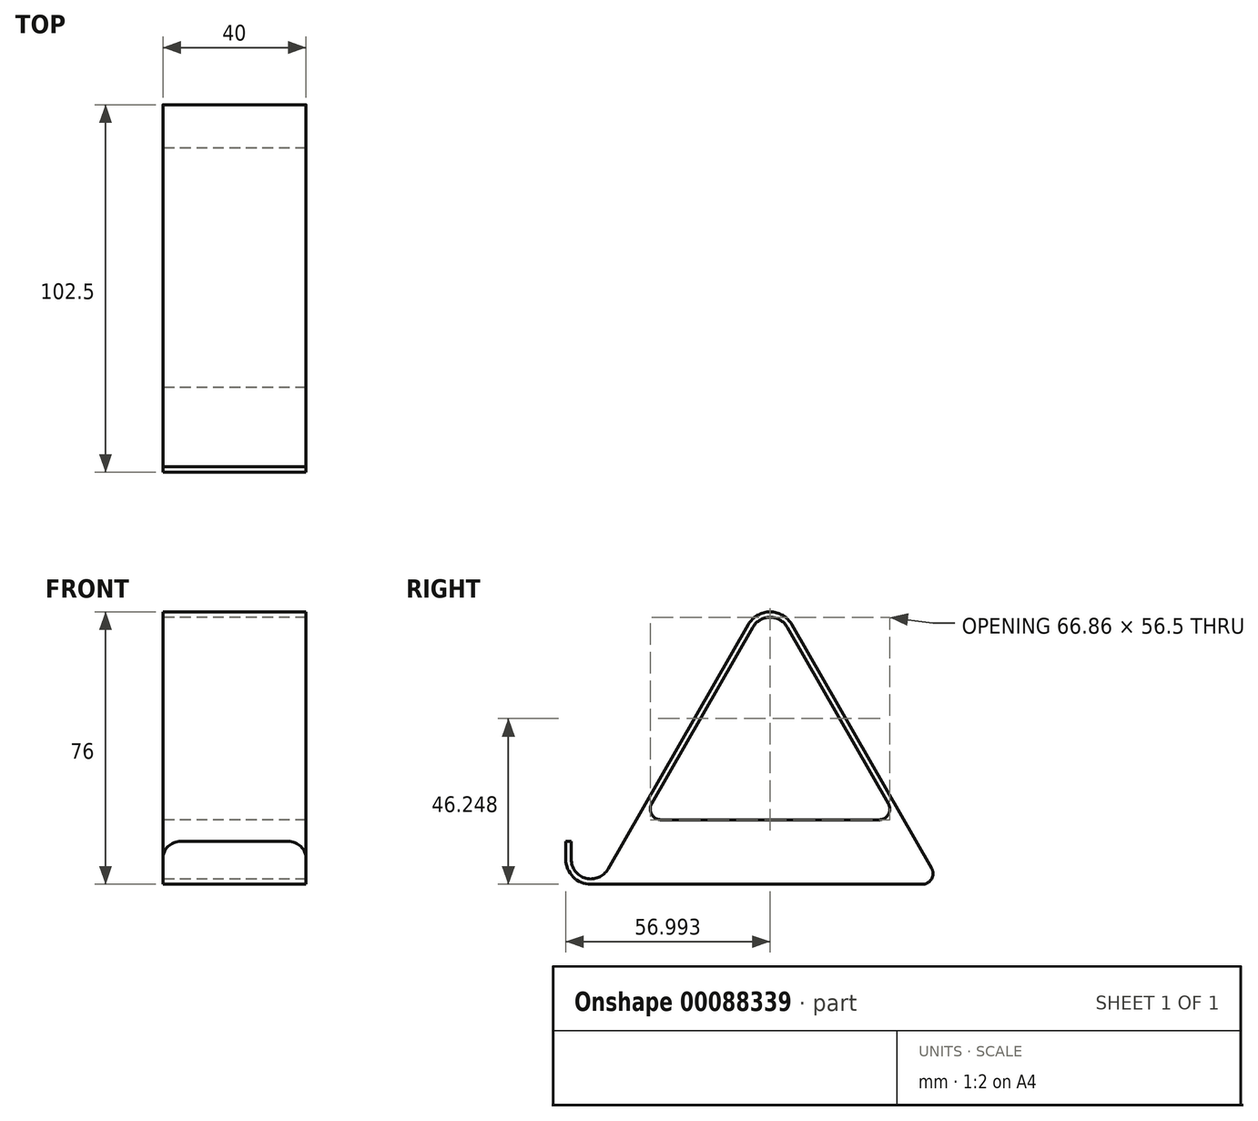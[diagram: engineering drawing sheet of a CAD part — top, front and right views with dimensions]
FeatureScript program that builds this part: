
annotation { "Feature Type Name" : "Feature", "Feature Type Description" : "" }
export const myFeature = defineFeature(function(context is Context, id is Id, definition is map)
    precondition{}
    {
        {
            var Q0;
            Q0=qCreatedBy(makeId("Right.planeOp"),FACE);
            var sketch = newSketch(context, id + "F0", { "sketchPlane" : qUnion([Q0])});
            skArc(sketch, "E0", {"start": v(54.77, 64.74) * mm, "mid": v(50, 67.5) * mm, "end": v(45.23, 64.74) * mm});
            skArc(sketch, "E1", {"start": v(-7, 0) * mm, "mid": v(-4.95, -4.95) * mm, "end": v(0, -7) * mm});
            skLineSegment(sketch, "E2", {"start": v(16.96, 15.49) * mm, "end": v(45.23, 64.74) * mm});
            skLineSegment(sketch, "E3", {"start": v(50, 62) * mm, "end": v(50, -33.54) * mm, "construction": true});
            skLineSegment(sketch, "E4", {"start": v(0, -7) * mm, "end": v(113.12, -7) * mm, "construction": true});
            skPoint(sketch, "E5.orphan", {"position": v(93.93, -3.48) * mm});
            skLineSegment(sketch, "E6", {"start": v(-7, 0) * mm, "end": v(-7, 5) * mm});
            skLineSegment(sketch, "E7.0", {"start": v(-5.5, 0) * mm, "end": v(-5.5, 5) * mm});
            skLineSegment(sketch, "E7.1", {"start": v(95.1, -2.5) * mm, "end": v(56.07, 65.48) * mm});
            skArc(sketch, "E7.2", {"start": v(56.07, 65.48) * mm, "mid": v(50, 69) * mm, "end": v(43.93, 65.48) * mm});
            skLineSegment(sketch, "E7.3", {"start": v(4.77, -2.74) * mm, "end": v(43.93, 65.48) * mm});
            skArc(sketch, "E7.4", {"start": v(-5.5, 0) * mm, "mid": v(-1.42, -5.31) * mm, "end": v(4.77, -2.74) * mm});
            skLineSegment(sketch, "E8", {"start": v(-7, 5) * mm, "end": v(-5.5, 5) * mm});
            skLineSegment(sketch, "E9", {"start": v(0, -7) * mm, "end": v(92.5, -7) * mm});
            skLineSegment(sketch, "E10.trimOffspring", {"start": v(19.56, 11) * mm, "end": v(80.42, 11) * mm});
            skPoint(sketch, "E11.orphan", {"position": v(6.07, -3.48) * mm});
            skLineSegment(sketch, "E12.trimOffspring", {"start": v(83.02, 15.49) * mm, "end": v(54.77, 64.74) * mm});
            skPoint(sketch, "E13.visualSharp", {"position": v(14.38, 11) * mm});
            skArc(sketch, "E13.filletArc", {"start": v(16.96, 15.49) * mm, "mid": v(16.97, 12.5) * mm, "end": v(19.56, 11) * mm});
            skPoint(sketch, "E14.visualSharp", {"position": v(85.6, 11) * mm});
            skArc(sketch, "E14.filletArc", {"start": v(80.42, 11) * mm, "mid": v(83.02, 12.5) * mm, "end": v(83.02, 15.49) * mm});
            skPoint(sketch, "E15.visualSharp", {"position": v(97.68, -7) * mm});
            skArc(sketch, "E15.filletArc", {"start": v(92.5, -7) * mm, "mid": v(95.1, -5.5) * mm, "end": v(95.1, -2.5) * mm});
            skSolve(sketch);
        }
        {
            var Q0;
            Q0=makeQuery(id+"F0.imprint","IMPRINT",FACE,{"disambiguationData":[TD([[makeQuery(id+"F0.imprint","IMPRINT",EDGE,{"derivedFrom":sQuery(id+"F0.wireOp",EDGE,"E0")}),-1.0]])]});
            extrude(context, id + "F1", {"entities" : qUnion([Q0]), "depth" : 40 * mm});
        }
        {
            var Q0;
            Q0=makeQuery(id+"F1.opExtrude","CAP_EDGE",EDGE,{"disambiguationData":[OSD([sQuery(id+"F0.wireOp",EDGE,"E8")])],"isStart":false});
            var Q1;
            Q1=makeQuery(id+"F1.opExtrude","CAP_EDGE",EDGE,{"disambiguationData":[OSD([sQuery(id+"F0.wireOp",EDGE,"E8")])],"isStart":true});
            fillet(context, id + "F2", {"entities" : qUnion([Q0, Q1]), "radius" : 5 * mm, "tangentPropagation" : true, "allowEdgeOverflow" : false});
        }
    });
